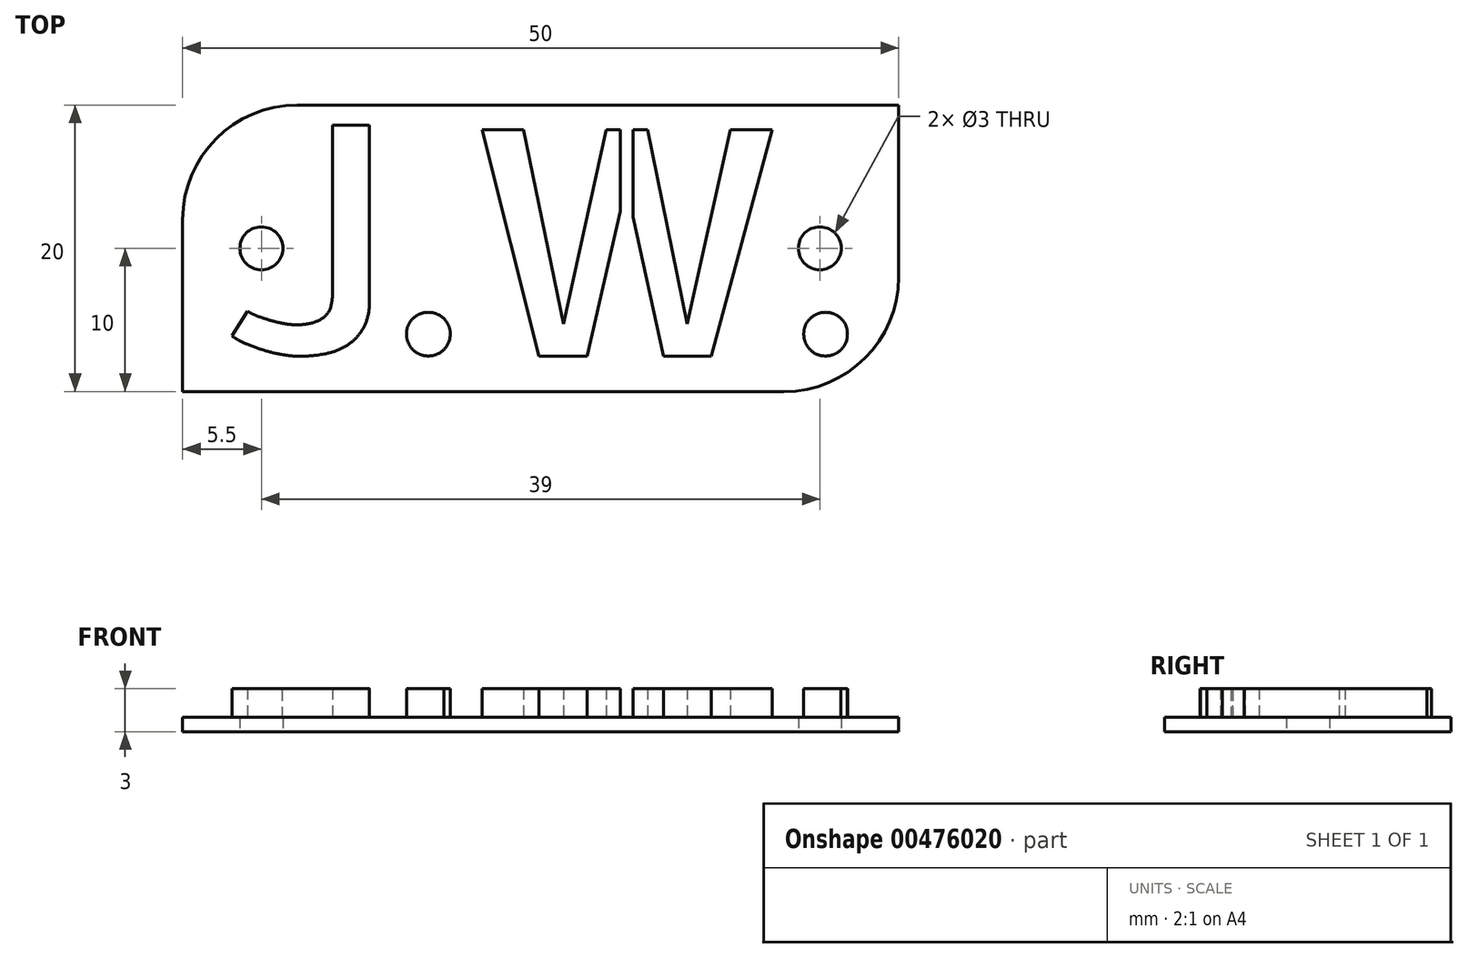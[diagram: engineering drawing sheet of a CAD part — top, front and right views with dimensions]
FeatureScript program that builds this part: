
annotation { "Feature Type Name" : "Feature", "Feature Type Description" : "" }
export const myFeature = defineFeature(function(context is Context, id is Id, definition is map)
    precondition{}
    {
        {
            var Q0;
            Q0=qCreatedBy(makeId("Top.planeOp"),FACE);
            var sketch = newSketch(context, id + "F0", { "sketchPlane" : qUnion([Q0])});
            skLineSegment(sketch, "E0.bottom", {"start": v(0, 0) * mm, "end": v(42, 0) * mm});
            skLineSegment(sketch, "E0.top", {"start": v(8, 20) * mm, "end": v(50, 20) * mm});
            skLineSegment(sketch, "E0.left", {"start": v(0, 0) * mm, "end": v(0, 12) * mm});
            skLineSegment(sketch, "E0.right", {"start": v(50, 8) * mm, "end": v(50, 20) * mm});
            skCircle(sketch, "E1", {"center": v(5.5, 10) * mm, "radius": 1.5 * mm});
            skPoint(sketch, "E1.centerSnap0", {"position": v(0, 10) * mm});
            skCircle(sketch, "E2", {"center": v(44.5, 10) * mm, "radius": 1.5 * mm});
            skPoint(sketch, "E3.visualSharp", {"position": v(0, 20) * mm});
            skArc(sketch, "E3.filletArc", {"start": v(8, 20) * mm, "mid": v(2.34, 17.66) * mm, "end": v(0, 12) * mm});
            skPoint(sketch, "E4.visualSharp", {"position": v(50, 0) * mm});
            skArc(sketch, "E4.filletArc", {"start": v(42, 0) * mm, "mid": v(47.66, 2.34) * mm, "end": v(50, 8) * mm});
            skSolve(sketch);
        }
        {
            var Q0;
            Q0=makeQuery(id+"F0.imprint","IMPRINT",FACE,{"disambiguationData":[TD([[makeQuery(id+"F0.imprint","IMPRINT",EDGE,{"derivedFrom":sQuery(id+"F0.wireOp",EDGE,"E0.bottom")}),1.0]])]});
            extrude(context, id + "F1", {"entities" : qUnion([Q0]), "depth" : 1 * mm});
        }
        {
            var Q0;
            Q0=makeQuery(id+"F1.opExtrude","CAP_FACE",FACE,{"disambiguationData":[OSD([sQuery(id+"F0.wireOp",EDGE,"E0.bottom"),sQuery(id+"F0.wireOp",EDGE,"E0.top"),sQuery(id+"F0.wireOp",EDGE,"E0.left"),sQuery(id+"F0.wireOp",EDGE,"E0.right"),sQuery(id+"F0.wireOp",EDGE,"E1"),sQuery(id+"F0.wireOp",EDGE,"E2"),sQuery(id+"F0.wireOp",EDGE,"E3.filletArc"),sQuery(id+"F0.wireOp",EDGE,"E4.filletArc")])],"isStart":false});
            var sketch = newSketch(context, id + "F2", { "sketchPlane" : qUnion([Q0])});
            skText(sketch, "E5", { "text": "J.W.", "fontName": "AllertaStencil-Regular.ttf"});
            const initialGuessF2  = {"E5": [0.00288, 0.00257, 1, 0, 0.01573]};
            skSetInitialGuess(sketch, initialGuessF2);
            skSolve(sketch);
        }
        {
            var Q0;
            Q0=makeQuery(id+"F2.imprint","IMPRINT",FACE,{"disambiguationData":[TD([[makeQuery(id+"F2.imprint","IMPRINT",EDGE,{"derivedFrom":sQuery(id+"F2.wireOp",EDGE,"E5.sketch_text.stroke-0")}),-1.0]])]});
            var Q1;
            Q1=makeQuery(id+"F2.imprint","IMPRINT",FACE,{"disambiguationData":[TD([[makeQuery(id+"F2.imprint","IMPRINT",EDGE,{"derivedFrom":sQuery(id+"F2.wireOp",EDGE,"E5.sketch_text.stroke-18")}),-1.0]])]});
            var Q2;
            Q2=makeQuery(id+"F2.imprint","IMPRINT",FACE,{"disambiguationData":[TD([[makeQuery(id+"F2.imprint","IMPRINT",EDGE,{"derivedFrom":sQuery(id+"F2.wireOp",EDGE,"E5.sketch_text.stroke-26")}),-1.0]])]});
            var Q3;
            Q3=makeQuery(id+"F2.imprint","IMPRINT",FACE,{"disambiguationData":[TD([[makeQuery(id+"F2.imprint","IMPRINT",EDGE,{"derivedFrom":sQuery(id+"F2.wireOp",EDGE,"E5.sketch_text.stroke-34")}),-1.0]])]});
            var Q4;
            Q4=makeQuery(id+"F2.imprint","IMPRINT",FACE,{"disambiguationData":[TD([[makeQuery(id+"F2.imprint","IMPRINT",EDGE,{"derivedFrom":sQuery(id+"F2.wireOp",EDGE,"E5.sketch_text.stroke-42")}),-1.0]])]});
            extrude(context, id + "F3", {"entities" : qUnion([Q0, Q1, Q2, Q3, Q4]), "operationType" : NewBodyOperationType.ADD, "depth" : 2 * mm});
        }
    });
